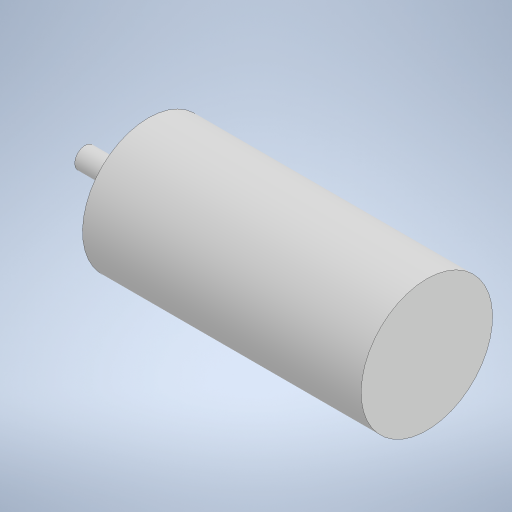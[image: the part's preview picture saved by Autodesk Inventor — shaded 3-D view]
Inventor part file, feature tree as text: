
AUTODESK INVENTOR PART (.ipt)
format: ipt  version: 2023 (Build 270158000, 158)  size: 223,744 bytes
history: native  units: mm
features: extrude x2, sketch x2, plane x1
ambient origin geometry x8: Origin, YZ Plane, XZ Plane, XY Plane, X Axis, Y Axis, Z Axis, Center Point
bodies: Volumenkörper1 (feature_tree)
feature tree (5):
  extrude  "Extrusion1"  Depth=53.0mm TaperAngle=0.0deg
  extrude  "Extrusion2"  Depth=12.0mm TaperAngle=0.0deg
  plane  "Arbeitsebene2"
  sketch  "Skizze2"  dims[d0=25.0mm d1=53.0mm d2=0.0mm]
  sketch  "Skizze3"  dims[d3=4.0mm d4=12.0mm d5=0.0mm d6=0.0mm]
